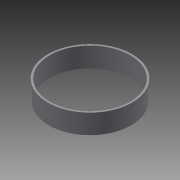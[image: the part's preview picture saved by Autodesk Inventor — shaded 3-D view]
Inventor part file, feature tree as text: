
AUTODESK INVENTOR PART (.ipt)
format: ipt  version: 2015 (Build 190159000, 159)  size: 101,376 bytes
history: native  units: in
note: dims shown in document units (in); Inventor stores cm internally (conversion verified against a paired STEP export)
features: revolve x1, sketch x1
ambient origin geometry x8: Origin, YZ Plane, XZ Plane, XY Plane, X Axis, Y Axis, Z Axis, Center Point
bodies: Solid1 (feature_tree)
feature tree (2):
  revolve  "Revolution1"  Angle=90.0deg
  sketch  "Sketch1"  dims[d0=1.25in d1=0.125in d2=1.125in d3=4.375in d4=0.125in d5=5.75in d6=0.125in d7=0.5in d8=1.625in d9=0.125in d10=90.0deg]
